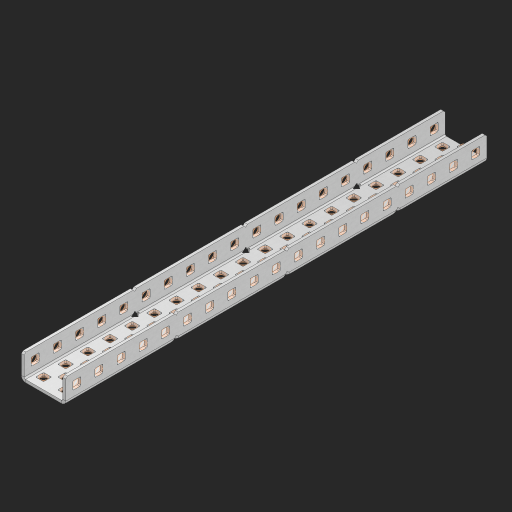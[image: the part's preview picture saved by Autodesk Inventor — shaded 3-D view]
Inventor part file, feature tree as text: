
AUTODESK INVENTOR PART (.ipt)
format: ipt  version: 2023 (Build 270158000, 158)  size: 1,342,464 bytes
history: native  units: in
note: dims shown in document units (in); Inventor stores cm internally (conversion verified against a paired STEP export)
features: other x102, extrude x93, sheet_metal_op x11, sketch x10, pattern_linear x2, mirror x1, chamfer x1
ambient origin geometry x8: Origin, YZ Plane, XZ Plane, XY Plane, X Axis, Y Axis, Z Axis, Center Point
bodies: Solid1 (feature_tree), Body (feature_tree)
feature tree (220):
  sheet_metal_op  "Flanges"
  other  "Flange Pattern Plane"
  other  "Flange Pattern Sketch"
  sheet_metal_op  "Flange Pattern"
  sheet_metal_op  "Body Pattern"
  pattern_linear  "Center Pattern"  Spacing1=0.0625in  [1 undecoded]
  other  "Arc Length"
  mirror  "Notch Mirror"
  pattern_linear  "Notch Pattern"  Spacing1=0.182in  [1 undecoded]
  chamfer  "End Chamfer"
  extrude  "Half Cut"  Depth=0.02in
  sketch  "Sketch1"  dims[d0=1.0in]
  other  "Plate1"
  sketch  "Sketch2"  dims[d1=9.5in]
  other  "Plate2"
  sheet_metal_op  "Bend1"
  sheet_metal_op  "Corner1"
  sketch  "Sketch3"  dims[d2=0.0625in]
  sketch  "Sketch7"  dims[d3=0.0625in]
  other  "Srf1"
  other  "Srf2"
  sketch  "Sketch8"  dims[d4=0.0312in]
  sketch  "Sketch9"  dims[d5=0.125in]
  other  "Srf91"
  sheet_metal_op  "Body Pattern Sketch"
  other  "Srf92"
  sketch  "Sketch13"  dims[d6=0.0625in]
  sketch  "Sketch14"  dims[d7=0.5in d8=90.0deg d9=0.0312in]
  sketch  "Sketch15"  dims[d10=0.25in]
  sketch  "Sketch16"  dims[d11=0.0625in d12=0.0625in d16=0.182in d17=0.02in d18=0.0625in d19=0.0in d20=0.25in d21=0.25in d38=7.4803in d40=0.5in d41=0.7874in d43=1.0in d46=0.172in d47=1.0in d48=0.0in d49=0.182in d50=0.02in d51=0.25in d52=0.25in d53=0.0625in d54=0.0in d55=0.172in d56=1.0in d57=0.0in d58=0.25in d60=7.4803in d62=0.5in d63=0.7874in d65=0.5in d85=0.1473in d86=0.1782in d88=0.04in d89=0.0625in d90=0.0in d91=0.04in d92=0.0491in d95=2.5in d96=0.04in d97=0.25in d98=45.0deg d99=0.25in d100=0.5in d101=0.0in d102=2.497in d106=0.182in d107=0.02in d108=0.5in d109=0.5in d110=0.0625in d111=0.0in d112=0.172in d113=0.5in d114=0.0in d117=0.5in d118=0.5in d119=0.5in]
  other  "Srf786"
  other  "Srf823"
  other  "Srf824"
  other  "Srf825"
  other  "Srf826"
  other  "Srf827"
  other  "Srf828"
  other  "Srf829"
  other  "Srf856"
  other  "Srf857"
  other  "Srf858"
  other  "Srf859"
  other  "Srf860"
  other  "Srf861"
  other  "Srf862"
  other  "Srf889"
  other  "Srf890"
  other  "Srf891"
  other  "Srf892"
  other  "Srf893"
  other  "Srf894"
  other  "Srf895"
  other  "Srf896"
  other  "Srf922"
  other  "Srf923"
  other  "Srf924"
  other  "Srf925"
  other  "Srf926"
  other  "Srf959"
  other  "Srf960"
  other  "Srf961"
  other  "Srf962"
  other  "Srf963"
  other  "Srf996"
  other  "Srf997"
  other  "Srf998"
  other  "Srf999"
  other  "Srf1000"
  other  "Srf1143"
  other  "Srf1144"
  other  "Srf1145"
  other  "Srf1146"
  other  "Srf1147"
  other  "Srf1148"
  other  "Srf1149"
  other  "Srf1150"
  other  "Srf1151"
  other  "Srf1152"
  other  "Srf1153"
  other  "Srf1154"
  other  "Srf1155"
  other  "Srf1156"
  other  "Srf1157"
  other  "Srf1158"
  other  "Srf1159"
  other  "Srf1160"
  other  "Srf1161"
  other  "Srf1162"
  other  "Srf1163"
  other  "Srf1164"
  other  "Srf1165"
  other  "Srf1166"
  other  "Srf1199"
  other  "Srf1200"
  other  "Srf1201"
  other  "Srf1202"
  other  "Srf1203"
  other  "Srf1204"
  other  "Srf1205"
  other  "Srf1206"
  other  "Srf1207"
  other  "Srf1208"
  other  "Srf1209"
  other  "Srf1210"
  other  "Srf1211"
  other  "Srf1212"
  other  "Srf1213"
  other  "Srf1214"
  other  "Srf1215"
  other  "Srf1216"
  other  "Srf1217"
  other  "Srf1218"
  other  "Srf1219"
  other  "Srf1220"
  other  "Srf1221"
  other  "Srf1222"
  other  "Srf1255"
  other  "Srf1256"
  other  "Srf1257"
  other  "Srf1258"
  other  "Srf1259"
  sheet_metal_op  "Flange Stamp"
  sheet_metal_op  "Flange Circle"
  sheet_metal_op  "Body Stamp"
  sheet_metal_op  "Body Circle"
  other  "Center Stamp"
  other  "Center Circle"
  sheet_metal_op  "Notch"
  extrude  "ExtrusionSrf2"  Depth=0.0625in
  extrude  "ExtrusionSrf92"  TaperAngle=0.0deg  [1 undecoded]
  extrude  "ExtrusionSrf823"  Depth=0.5in
  extrude  "ExtrusionSrf824"  Depth=0.5in
  extrude  "ExtrusionSrf825"  Depth=0.5in
  extrude  "ExtrusionSrf826"  Depth=0.5in
  extrude  "ExtrusionSrf827"  Depth=1.0in TaperAngle=0.0deg
  extrude  "ExtrusionSrf828"  Depth=0.5in
  extrude  "ExtrusionSrf829"  Depth=0.02in
  extrude  "ExtrusionSrf856"  Depth=0.5in
  extrude  "ExtrusionSrf857"  Depth=0.5in
  extrude  "ExtrusionSrf858"  Depth=0.0625in
  extrude  "ExtrusionSrf859"  TaperAngle=0.0deg  [1 undecoded]
  extrude  "ExtrusionSrf860"  Depth=0.5in
  extrude  "ExtrusionSrf861"  Depth=1.0in TaperAngle=0.0deg
  extrude  "ExtrusionSrf862"  Depth=0.5in
  extrude  "ExtrusionSrf889"  Depth=0.5in
  extrude  "ExtrusionSrf890"  Depth=0.5in
  extrude  "ExtrusionSrf891"  Depth=0.5in
  extrude  "ExtrusionSrf892"  Depth=0.5in
  extrude  "ExtrusionSrf893"  Depth=0.5in
  extrude  "ExtrusionSrf894"  Depth=0.0625in
  extrude  "ExtrusionSrf895"  TaperAngle=0.0deg  [1 undecoded]
  extrude  "ExtrusionSrf896"  Depth=0.5in
  extrude  "ExtrusionSrf922"  Depth=0.5in
  extrude  "ExtrusionSrf923"  Depth=2.5in
  extrude  "ExtrusionSrf924"  Depth=0.5in TaperAngle=45.0deg
  extrude  "ExtrusionSrf925"  Depth=0.5in
  extrude  "ExtrusionSrf926"  Depth=0.5in TaperAngle=0.0deg
  extrude  "ExtrusionSrf959"  Depth=0.5in
  extrude  "ExtrusionSrf960"  Depth=0.5in
  extrude  "ExtrusionSrf961"  Depth=0.02in
  extrude  "ExtrusionSrf962"  Depth=0.5in
  extrude  "ExtrusionSrf963"  Depth=0.5in
  extrude  "ExtrusionSrf996"  Depth=0.0625in
  extrude  "ExtrusionSrf997"  TaperAngle=0.0deg  [1 undecoded]
  extrude  "ExtrusionSrf998"  Depth=0.5in
  extrude  "ExtrusionSrf999"  Depth=0.5in TaperAngle=0.0deg
  extrude  "ExtrusionSrf1000"  Depth=0.5in
  extrude  "ExtrusionSrf1143"  Depth=0.5in
  extrude  "ExtrusionSrf1144"  Depth=0.5in
  extrude  "ExtrusionSrf1145"  [1 undecoded]
  extrude  "ExtrusionSrf1146"  [1 undecoded]
  extrude  "ExtrusionSrf1147"  [1 undecoded]
  extrude  "ExtrusionSrf1148"  [1 undecoded]
  extrude  "ExtrusionSrf1149"  [1 undecoded]
  extrude  "ExtrusionSrf1150"  [1 undecoded]
  extrude  "ExtrusionSrf1151"  [1 undecoded]
  extrude  "ExtrusionSrf1152"  [1 undecoded]
  extrude  "ExtrusionSrf1153"  [1 undecoded]
  extrude  "ExtrusionSrf1154"  [1 undecoded]
  extrude  "ExtrusionSrf1155"  [1 undecoded]
  extrude  "ExtrusionSrf1156"  [1 undecoded]
  extrude  "ExtrusionSrf1157"  [1 undecoded]
  extrude  "ExtrusionSrf1158"  [1 undecoded]
  extrude  "ExtrusionSrf1159"  [1 undecoded]
  extrude  "ExtrusionSrf1160"  [1 undecoded]
  extrude  "ExtrusionSrf1161"  [1 undecoded]
  extrude  "ExtrusionSrf1162"  [1 undecoded]
  extrude  "ExtrusionSrf1163"  [1 undecoded]
  extrude  "ExtrusionSrf1164"  [1 undecoded]
  extrude  "ExtrusionSrf1165"  [1 undecoded]
  extrude  "ExtrusionSrf1166"  [1 undecoded]
  extrude  "ExtrusionSrf1199"  [1 undecoded]
  extrude  "ExtrusionSrf1200"  [1 undecoded]
  extrude  "ExtrusionSrf1201"  [1 undecoded]
  extrude  "ExtrusionSrf1202"  [1 undecoded]
  extrude  "ExtrusionSrf1203"  [1 undecoded]
  extrude  "ExtrusionSrf1204"  [1 undecoded]
  extrude  "ExtrusionSrf1205"  [1 undecoded]
  extrude  "ExtrusionSrf1206"  [1 undecoded]
  extrude  "ExtrusionSrf1207"  [1 undecoded]
  extrude  "ExtrusionSrf1208"  [1 undecoded]
  extrude  "ExtrusionSrf1209"  [1 undecoded]
  extrude  "ExtrusionSrf1210"  [1 undecoded]
  extrude  "ExtrusionSrf1211"  [1 undecoded]
  extrude  "ExtrusionSrf1212"  [1 undecoded]
  extrude  "ExtrusionSrf1213"  [1 undecoded]
  extrude  "ExtrusionSrf1214"  [1 undecoded]
  extrude  "ExtrusionSrf1215"  [1 undecoded]
  extrude  "ExtrusionSrf1216"  [1 undecoded]
  extrude  "ExtrusionSrf1217"  [1 undecoded]
  extrude  "ExtrusionSrf1218"  [1 undecoded]
  extrude  "ExtrusionSrf1219"  [1 undecoded]
  extrude  "ExtrusionSrf1220"  [1 undecoded]
  extrude  "ExtrusionSrf1221"  [1 undecoded]
  extrude  "ExtrusionSrf1222"  [1 undecoded]
  extrude  "ExtrusionSrf1255"  [1 undecoded]
  extrude  "ExtrusionSrf1256"  [1 undecoded]
  extrude  "ExtrusionSrf1257"  [1 undecoded]
  extrude  "ExtrusionSrf1258"  [1 undecoded]
  extrude  "ExtrusionSrf1259"  [1 undecoded]
note: 57 required parameter values undecoded (feature->parameter linkage not recoverable at this tier; creation-order binding heuristic only, values carry confidence <= 0.55)
